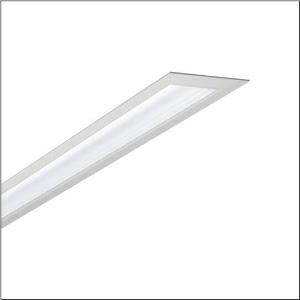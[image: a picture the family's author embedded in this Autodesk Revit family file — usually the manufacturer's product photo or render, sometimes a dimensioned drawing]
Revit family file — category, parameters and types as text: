
# Revit family: silica_r_5mx11bd1w4a_3352
name_source: partatom
category: Lighting Fixtures
units: mm (PartAtom-declared; Revit-internal decimal feet)

## family parameters
Cut with Voids When Loaded = No
Host = Face
Light Source = No
Part Type = Normal
Room Calculation Point = No
Round Connector Dimension = Use Diameter
Shared = No

## types (1)
- --- (1 x LED, 4950 lm, 29.3 W, 4000K)
    Apparent Load = 29 VA
    CIE Flux Codes = 82 97 100 100 100
    Color Rendering = 80
    Color Temperature = 4000K
    Default Elevation = 1800 mm
    Description = Silica®, office luminaire, of aluminium, light emission: direct distribution, primary light characteristic: symmetric, installation type: recessed, LED, rated luminous flux: 4.950lm, luminous efficacy: 169lm/W, light colour: 840, colour temperature: 4000K, control gear: ECG DALI, with terminal, 3+2-pole, max. 2.5mm², mains connection: 230V, AC, 50/60Hz, rated input power: 29W, luminaire housing, of aluminium, matt pure white (RAL 9010), length: 1.462mm, width: 93mm, height: 60mm, end cap, of diecast zinc, pure white (RAL 9010), protection rating (complete): IP20, insulation class (complete): insulation class I (protective earthing), certification: CE, permissible operating ambient temperature: 0..+35°C, standard: EN 50419, packaging unit: 1 piece
    Height = 0 mm  [stored 0 ft]
    Lamp = 1 x LED
    Lamp Light Flux = 4950 lm
    Lamp Power = 29.3 W
    Lamp count = 1
    Length = 1462 mm
    Luminous efficacy = 169 lm/W
    Manufacturer = Siteco
    ModVariant = No
    Model = 5MX11BD1W4A
    Mounting Place = Ceiling
    Mounting Type = Recessed
    Number of Poles = 1
    OnlyDefault = Yes
    Power Factor = 1
    Product Name = Silica®
    Product group = office luminaire | ceiling recessed
    ProductGroupID = 401
    Protection Class = Protection class I
    Protection Degree = IP 20
    RLX_Detail_Level = 1
    RLX_Emergency_Light_Flux = 0 lm
    RLX_Emergency_Type = 0
    RLX_Emergency_Type_DB = No
    RlxData = <blob elided: 24025 chars, md5=6d8687e1>
    Socket = socket
    Standby Power = 0 W
    System Light Flux = 4950 lm
    System Power = 29 W
    Type Comments = factory setting: luminous flux: 100 % | dim-lin: 254 | 163 mA
    Type Image = l_1004825.jpg
    URL = http://relux.com
    VarID = @adj_138554
    Voltage = 0 V
    Weight = 0.00 kg
    Width = 93 mm

note: [stored X ft] marks values corroborated as IEEE doubles in the binary element streams (Revit-internal decimal feet)

## geometry (parser evidence)
native form markers: Blend x4, Sweep x11
no freeform markers — native parametric forms only
